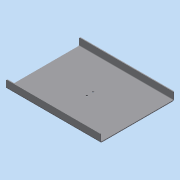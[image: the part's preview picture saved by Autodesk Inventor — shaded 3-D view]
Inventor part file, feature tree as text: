
AUTODESK INVENTOR PART (.ipt)
format: ipt  version: 2018 (Build 220112000, 112)  size: 159,232 bytes
history: native  units: mm
features: other x13, reference x6, sketch x3, hole x1
ambient origin geometry x8: Origin, YZ Plane, XZ Plane, XY Plane, X Axis, Y Axis, Z Axis, Center Point
bodies: Volumenkörper1 (feature_tree)
feature tree (23):
  other  "Fläche1"
  other  "Lasche1"
  hole  "Bohrung1"  [1 undecoded]
  other  "Eckenrundung1"
  sketch  "Skizze1"  dims[d0=230.0mm d1=180.0mm]
  other  "Grobblech1"
  sketch  "Skizze2"  dims[d2=2.0mm]
  other  "Grobblech2"
  other  "Biegung1"
  other  "Ecke1"
  sketch  "Skizze3"  dims[d3=2.0mm d4=1.0mm d5=4.0mm d6=2.0mm d7=20.0mm d8=90.0deg d9=2.0mm d10=8.0mm d11=2.0mm d12=2.0mm d13=3.0mm d14=4.0mm d15=6.0mm d16=4.0mm d17=2.0mm d18=90.0deg d19=2.0mm d20=20.594885mm]
  reference  "Referenz1"
  reference  "Referenz2"
  reference  "Referenz3"
  reference  "Referenz4"
  reference  "Referenz5"
  reference  "Referenz6"
  other  "Definition1"
  other  "<userpath>\Documents\Waage\CAD\Main.iam"
  other  "Main.iam"
  other  "LoadCell:2"
  other  "LoadCell:3"
  other  "LoadCell:1"
note: 1 required parameter value undecoded (feature->parameter linkage not recoverable at this tier; creation-order binding heuristic only, values carry confidence <= 0.55)
